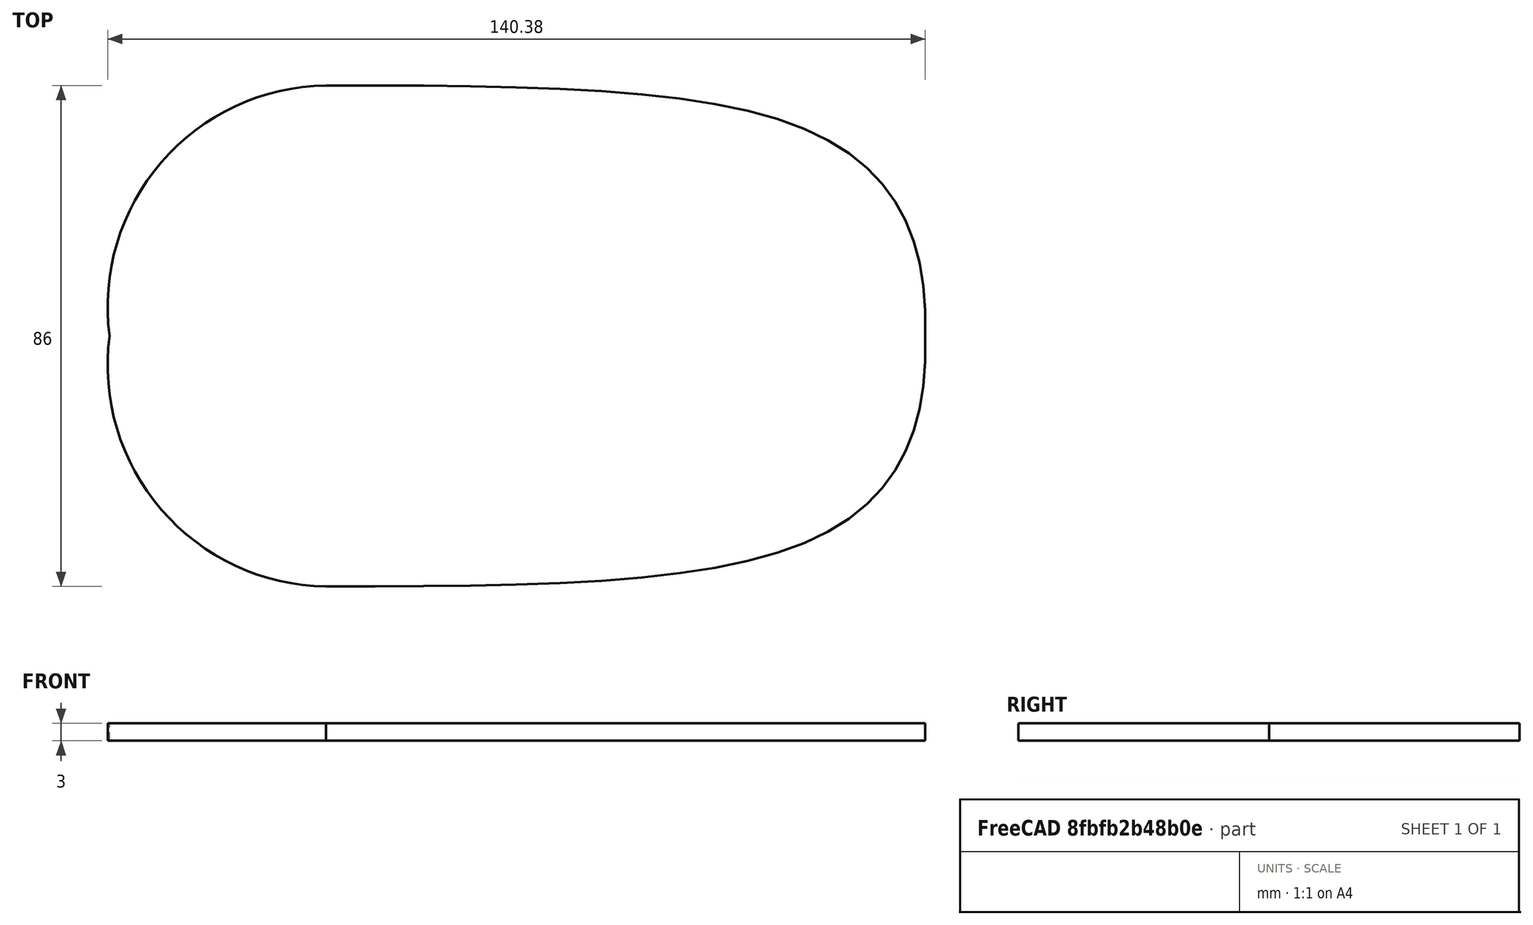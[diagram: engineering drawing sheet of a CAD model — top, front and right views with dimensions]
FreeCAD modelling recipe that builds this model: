
FCSTD DOCUMENT  (FreeCAD 0.17R13519 (Git))
Label: ChongJiZuan-jwei-1.0
License: All rights reserved
LicenseURL: http://en.wikipedia.org/wiki/All_rights_reserved
objects: Sketcher::SketchObject×1, PartDesign::Pad×1, PartDesign::Mirrored×1, PartDesign::Body×1
note: 5 computed .brp shape members not serialized (recipe doc carries the construction recipe); baked Part::Feature solids carry a one-line shape summary decoded from their .brp

FEATURE [Sketcher::SketchObject] Sketch
  MapMode = 5
  Support = -> [XY_Plane]
  sketch-geometry (17):
    g0: LineSegment StartX=-70 StartY=0 StartZ=0 EndX=70 EndY=0 EndZ=0
    g1: GeomPoint X=-69.9962 Y=-0.000265 Z=0
    g2-g6: Circle [constr] x5 (B-spline internal-alignment scaffolding for g7; pole/knot coordinates omitted)
    g7: BSplineCurve PolesCount=5 KnotsCount=3 Degree=3 IsPeriodic=0
    g8: GeomPoint [constr] X=-32.8591 Y=-43 Z=0
    g9: GeomPoint [constr] X=47.0138 Y=-36.4321 Z=0
    g10: GeomPoint [constr] X=70 Y=0 Z=0
    g11: ArcOfCircle CenterX=-32.3309 CenterY=-5.00367 CenterZ=0 NormalX=0 NormalY=0 NormalZ=1 AngleXU=0 Radius=38 StartAngle=3.00953 EndAngle=4.69849
    g12: Circle [constr] CenterX=-32.8591 CenterY=-38 CenterZ=0 NormalX=0 NormalY=0 NormalZ=1 AngleXU=0 Radius=6
    g13: Circle [constr] CenterX=0 CenterY=-38 CenterZ=0 NormalX=0 NormalY=0 NormalZ=1 AngleXU=0 Radius=6
    g14: Circle [constr] CenterX=58.6907 CenterY=-37.7504 CenterZ=0 NormalX=0 NormalY=0 NormalZ=1 AngleXU=0 Radius=6
    g15: Circle [constr] CenterX=65.9637 CenterY=-15.5497 CenterZ=0 NormalX=0 NormalY=0 NormalZ=1 AngleXU=0 Radius=6
    g16: Circle [constr] CenterX=65 CenterY=-5 CenterZ=0 NormalX=0 NormalY=0 NormalZ=1 AngleXU=0 Radius=6
  constraints (25):
    c: Horizontal(g0)
    c: DistanceX(g0,g0) = 140
    c: DistanceX(g-2,g0) = 70
    c: PointOnObject(g0,g-1)
    c: Radius(g2) = 4
    c: Equal(g2, g3-g6) x4
    c: InternalAlignment(g2-g6 -> g7) x5
    c: InternalAlignment(g8,g7)
    c: InternalAlignment(g9,g7)
    c: InternalAlignment(g10,g7)
    c: Coincident(g11,g0)
    c: Radius(g11) = 38
    c: Distance(g11,g0) = 43
    c: Coincident(g2,g11)
    c: Coincident(g6,g0)
    c: DistanceX(g-2,g16) = 65
    c: Vertical(g12,g2)
    c: Distance(g12,g2) = 5
    c: Radius(g12) = 6
    c: Equal(g12, g13-g16) x4
    c: PointOnObject(g13,g-2)
    c: Distance(g13,g3) = 5
    c: Vertical(g14,g4)
    c: Distance(g14,g4) = 5
    c: Distance(g15,g5) = 5
FEATURE [PartDesign::Pad] Pad
  Length = 3
  Length2 = 100
  Profile = -> Sketch
  Type = 0
FEATURE [PartDesign::Mirrored] Mirrored
  BaseFeature = -> Pad
  MirrorPlane = -> XZ_Plane
  Originals = -> [Pad]
FEATURE [PartDesign::Body] Body
  Group = -> [Sketch,Pad,Mirrored]
  Origin = -> Origin
  Tip = -> Mirrored
